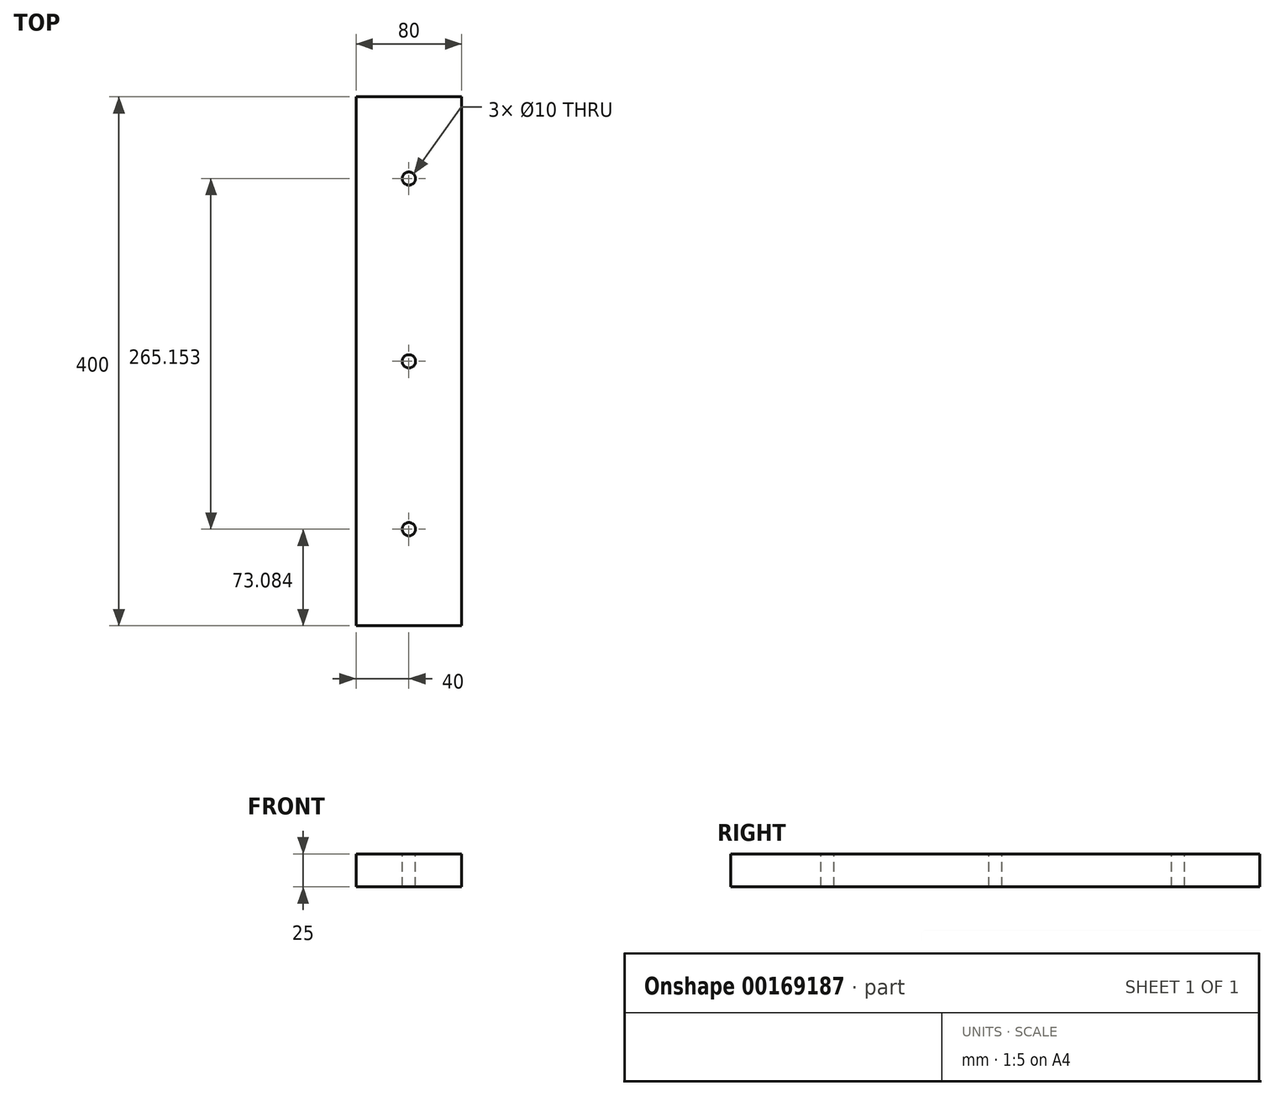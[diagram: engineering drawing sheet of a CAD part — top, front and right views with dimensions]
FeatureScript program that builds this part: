
annotation { "Feature Type Name" : "Feature", "Feature Type Description" : "" }
export const myFeature = defineFeature(function(context is Context, id is Id, definition is map)
    precondition{}
    {
        {
            var Q0;
            Q0=qCreatedBy(makeId("Top.planeOp"),FACE);
            var sketch = newSketch(context, id + "F0", { "sketchPlane" : qUnion([Q0])});
            skLineSegment(sketch, "E0.bottom", {"start": v(40, -200) * mm, "end": v(-40, -200) * mm});
            skLineSegment(sketch, "E0.top", {"start": v(40, 200) * mm, "end": v(-40, 200) * mm});
            skLineSegment(sketch, "E0.left", {"start": v(40, -200) * mm, "end": v(40, 200) * mm});
            skLineSegment(sketch, "E0.right", {"start": v(-40, -200) * mm, "end": v(-40, 200) * mm});
            skPoint(sketch, "E0.middle", {"position": v(0, 0) * mm});
            skSolve(sketch);
        }
        {
            var Q0;
            Q0=makeQuery(id+"F0.imprint","IMPRINT",FACE,{"disambiguationData":[TD([[makeQuery(id+"F0.imprint","IMPRINT",EDGE,{"derivedFrom":sQuery(id+"F0.wireOp",EDGE,"E0.bottom")}),-1.0]])]});
            extrude(context, id + "F1", {"entities" : qUnion([Q0]), "depth" : 25 * mm});
        }
        {
            var Q0;
            Q0=makeQuery(id+"F1.opExtrude","CAP_FACE",FACE,{"disambiguationData":[OSD([sQuery(id+"F0.wireOp",EDGE,"E0.bottom"),sQuery(id+"F0.wireOp",EDGE,"E0.top"),sQuery(id+"F0.wireOp",EDGE,"E0.left"),sQuery(id+"F0.wireOp",EDGE,"E0.right")])],"isStart":false});
            var sketch = newSketch(context, id + "F2", { "sketchPlane" : qUnion([Q0])});
            skPoint(sketch, "E1", {"position": v(0, 0) * mm});
            skPoint(sketch, "E2", {"position": v(0, -126.92) * mm});
            skPoint(sketch, "E2.positionSnap0", {"position": v(0, -200) * mm});
            skPoint(sketch, "E3", {"position": v(0, 138.24) * mm});
            skPoint(sketch, "E3.positionSnap0", {"position": v(0, 200) * mm});
            skSolve(sketch);
        }
        {
            var Q0;
            Q0=sQuery(id+"F2.wireOp",VERTEX,"E3");
            var Q1;
            Q1=sQuery(id+"F2.wireOp",VERTEX,"E1");
            var Q2;
            Q2=sQuery(id+"F2.wireOp",VERTEX,"E2");
            var Q3;
            Q3=makeQuery(id+"F1.opExtrude","SWEPT_BODY",BODY,{"disambiguationData":[OSD([sQuery(id+"F0.wireOp",EDGE,"E0.bottom"),sQuery(id+"F0.wireOp",EDGE,"E0.top"),sQuery(id+"F0.wireOp",EDGE,"E0.left"),sQuery(id+"F0.wireOp",EDGE,"E0.right")])]});
            hole(context, id + "F3", {"style" : HoleStyle.SIMPLE, "endStyle" : HoleEndStyle.THROUGH, "holeDiameter" : 10 * mm, "locations" : qUnion([Q0, Q1, Q2]), "scope" : qUnion([Q3]), "isTappedThrough" : true});
        }
    });
